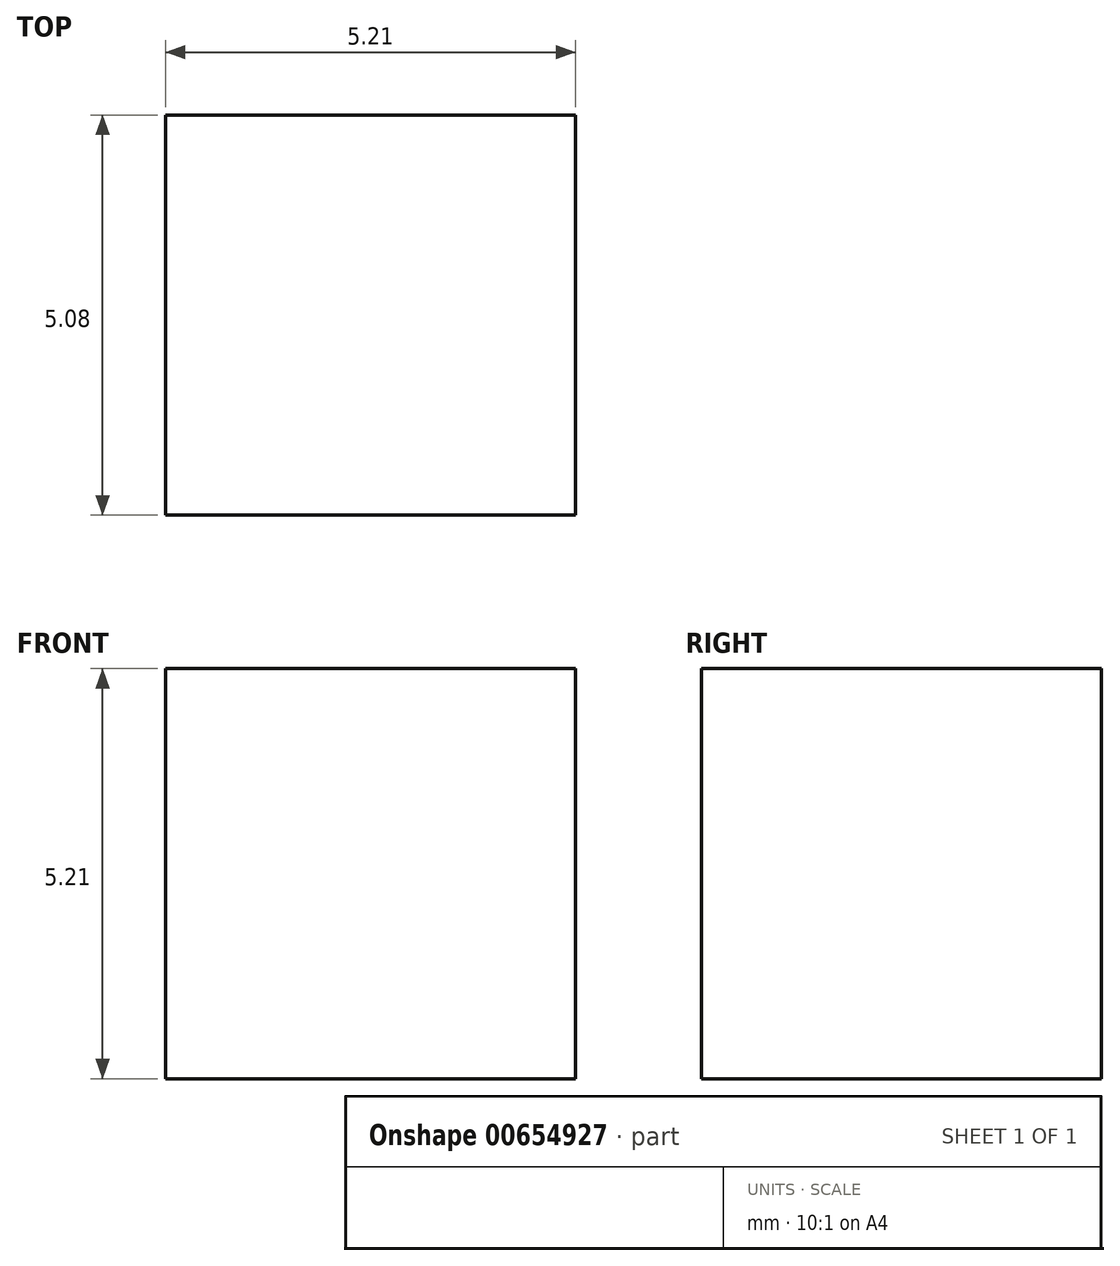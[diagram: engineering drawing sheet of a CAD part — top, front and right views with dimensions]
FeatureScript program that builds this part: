
annotation { "Feature Type Name" : "Feature", "Feature Type Description" : "" }
export const myFeature = defineFeature(function(context is Context, id is Id, definition is map)
    precondition{}
    {
        {
            var Q0;
            Q0=qCreatedBy(makeId("Front.planeOp"),FACE);
            var sketch = newSketch(context, id + "F0", { "sketchPlane" : qUnion([Q0])});
            skLineSegment(sketch, "E0", {"start": v(0, 0) * mm, "end": v(5.2, 0) * mm});
            skLineSegment(sketch, "E1", {"start": v(5.2, 0) * mm, "end": v(5.2, 5.2) * mm});
            skLineSegment(sketch, "E2", {"start": v(5.2, 5.2) * mm, "end": v(0, 5.2) * mm});
            skLineSegment(sketch, "E3", {"start": v(0, 5.2) * mm, "end": v(0, 0) * mm});
            skSolve(sketch);
        }
        {
            var Q0;
            Q0=makeQuery(id+"F0.imprint","IMPRINT",FACE,{"disambiguationData":[TD([[makeQuery(id+"F0.imprint","IMPRINT",EDGE,{"derivedFrom":sQuery(id+"F0.wireOp",EDGE,"E1")}),1.0]])]});
            extrude(context, id + "F1", {"entities" : qUnion([Q0]), "depth" : 5.08 * mm, "offsetDistance" : 25.4 * mm});
        }
    });
